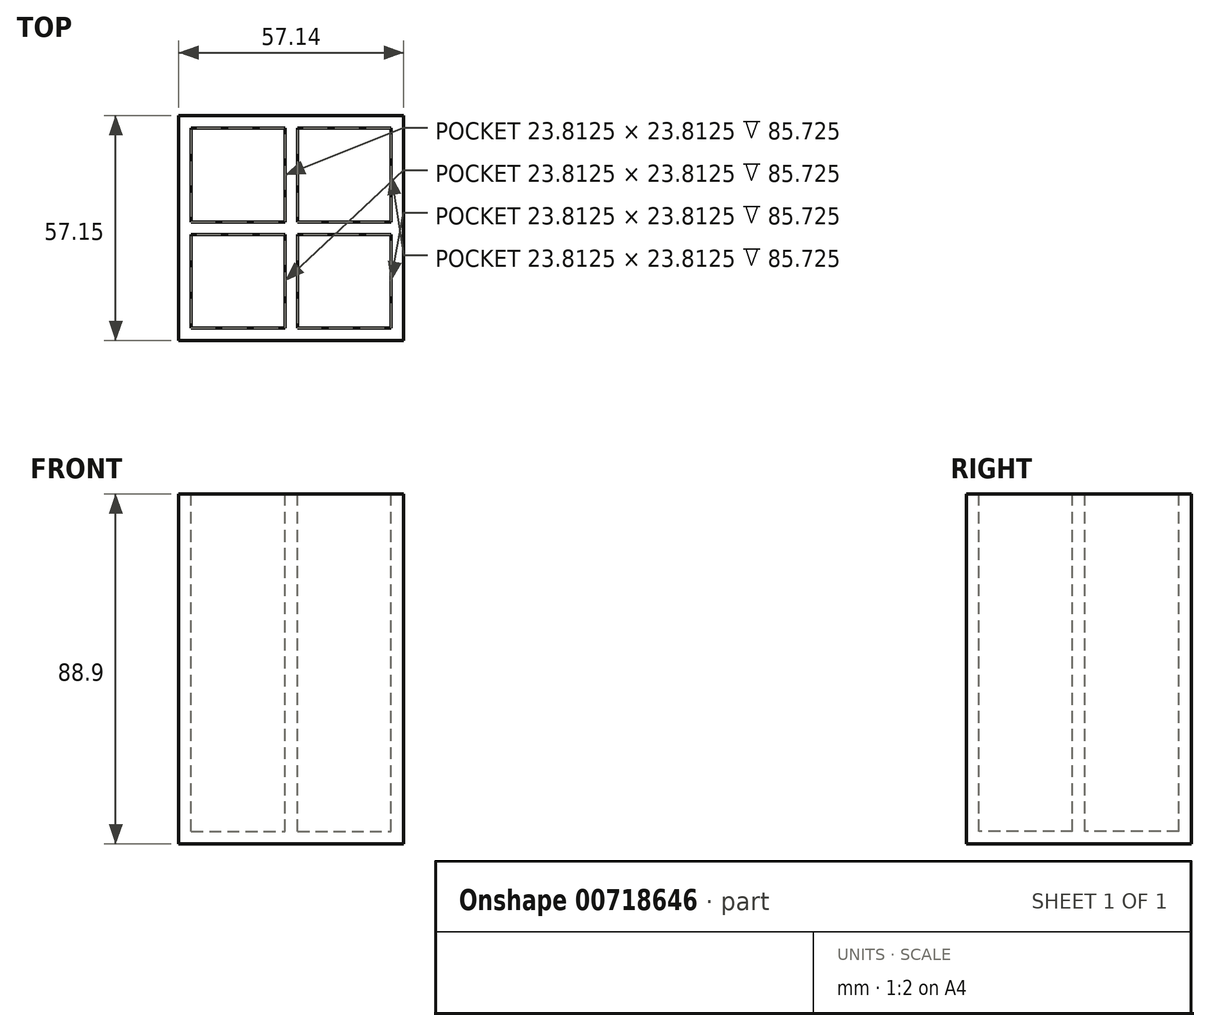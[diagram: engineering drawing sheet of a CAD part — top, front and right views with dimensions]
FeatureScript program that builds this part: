
annotation { "Feature Type Name" : "Feature", "Feature Type Description" : "" }
export const myFeature = defineFeature(function(context is Context, id is Id, definition is map)
    precondition{}
    {
        {
            var Q0;
            Q0=qCreatedBy(makeId("Front.planeOp"),FACE);
            var sketch = newSketch(context, id + "F0", { "sketchPlane" : qUnion([Q0])});
            skLineSegment(sketch, "E0.bottom", {"start": v(28.57, 44.45) * mm, "end": v(-28.58, 44.45) * mm});
            skLineSegment(sketch, "E0.top", {"start": v(28.58, -44.45) * mm, "end": v(-28.57, -44.45) * mm});
            skLineSegment(sketch, "E0.left", {"start": v(28.57, 44.45) * mm, "end": v(28.58, -44.45) * mm});
            skLineSegment(sketch, "E0.right", {"start": v(-28.58, 44.45) * mm, "end": v(-28.57, -44.45) * mm});
            skPoint(sketch, "E0.middle", {"position": v(0, 0) * mm});
            skSolve(sketch);
        }
        {
            var Q0;
            Q0=makeQuery(id+"F0.imprint","IMPRINT",FACE,{"disambiguationData":[TD([[makeQuery(id+"F0.imprint","IMPRINT",EDGE,{"derivedFrom":sQuery(id+"F0.wireOp",EDGE,"E0.bottom")}),1.0]])]});
            extrude(context, id + "F1", {"entities" : qUnion([Q0]), "depth" : 3.17 * mm, "offsetDistance" : 25.4 * mm});
        }
        {
            var Q0;
            Q0=makeQuery(id+"F1.opExtrude","CAP_FACE",FACE,{"disambiguationData":[OSD([sQuery(id+"F0.wireOp",EDGE,"E0.bottom"),sQuery(id+"F0.wireOp",EDGE,"E0.top"),sQuery(id+"F0.wireOp",EDGE,"E0.left"),sQuery(id+"F0.wireOp",EDGE,"E0.right")])],"isStart":true});
            extrude(context, id + "F2", {"entities" : qUnion([Q0]), "operationType" : NewBodyOperationType.ADD, "oppositeDirection" : true, "depth" : 57.15 * mm, "offsetDistance" : 25.4 * mm});
        }
        {
            var Q0;
            {var subQ0=sQuery(id+"F0.wireOp",EDGE,"E0.bottom");Q0=makeQuery(id+"F2.boolean.opBoolean","MERGE",FACE,{"derivedFrom":[makeQuery(id+"F1.opExtrude","SWEPT_FACE",FACE,{"disambiguationData":[OSD([subQ0])]}),makeQuery(id+"F2.opExtrude","SWEPT_FACE",FACE,{"disambiguationData":[OSD([subQ0])]})]});}
            var sketch = newSketch(context, id + "F3", { "sketchPlane" : qUnion([Q0])});
            skLineSegment(sketch, "E1.bottom", {"start": v(-25.4, -3.18) * mm, "end": v(-1.59, -3.18) * mm});
            skLineSegment(sketch, "E1.top", {"start": v(-25.4, -26.99) * mm, "end": v(-1.59, -26.99) * mm});
            skLineSegment(sketch, "E1.left", {"start": v(-25.4, -3.18) * mm, "end": v(-25.4, -26.99) * mm});
            skLineSegment(sketch, "E1.right", {"start": v(-1.59, -3.17) * mm, "end": v(-1.59, -26.99) * mm});
            skSolve(sketch);
        }
        {
            var Q0;
            Q0=makeQuery(id+"F3.imprint","IMPRINT",FACE,{"disambiguationData":[TD([[makeQuery(id+"F3.imprint","IMPRINT",EDGE,{"derivedFrom":sQuery(id+"F3.wireOp",EDGE,"E1.bottom")}),1.0]])]});
            var sketch = newSketch(context, id + "F4", { "sketchPlane" : qUnion([Q0])});
            skLineSegment(sketch, "E2.bottom", {"start": v(1.59, -3.18) * mm, "end": v(25.4, -3.18) * mm});
            skLineSegment(sketch, "E2.top", {"start": v(1.59, -26.99) * mm, "end": v(25.4, -26.99) * mm});
            skLineSegment(sketch, "E2.left", {"start": v(1.59, -3.18) * mm, "end": v(1.59, -26.99) * mm});
            skLineSegment(sketch, "E2.right", {"start": v(25.4, -3.17) * mm, "end": v(25.4, -26.99) * mm});
            skSolve(sketch);
        }
        {
            var Q0;
            Q0=makeQuery(id+"F3.imprint","IMPRINT",FACE,{"disambiguationData":[TD([[makeQuery(id+"F3.imprint","IMPRINT",EDGE,{"derivedFrom":sQuery(id+"F3.wireOp",EDGE,"E1.bottom")}),1.0]])]});
            var sketch = newSketch(context, id + "F5", { "sketchPlane" : qUnion([Q0])});
            skLineSegment(sketch, "E3.bottom", {"start": v(-25.4, -30.16) * mm, "end": v(-1.59, -30.16) * mm});
            skLineSegment(sketch, "E3.top", {"start": v(-25.4, -53.98) * mm, "end": v(-1.59, -53.98) * mm});
            skLineSegment(sketch, "E3.left", {"start": v(-25.4, -30.16) * mm, "end": v(-25.4, -53.98) * mm});
            skLineSegment(sketch, "E3.right", {"start": v(-1.59, -30.16) * mm, "end": v(-1.59, -53.98) * mm});
            skSolve(sketch);
        }
        {
            var Q0;
            Q0=makeQuery(id+"F3.imprint","IMPRINT",FACE,{"disambiguationData":[TD([[makeQuery(id+"F3.imprint","IMPRINT",EDGE,{"derivedFrom":sQuery(id+"F3.wireOp",EDGE,"E1.bottom")}),1.0]])]});
            var sketch = newSketch(context, id + "F6", { "sketchPlane" : qUnion([Q0])});
            skLineSegment(sketch, "E4.bottom", {"start": v(1.59, -30.16) * mm, "end": v(25.4, -30.16) * mm});
            skLineSegment(sketch, "E4.top", {"start": v(1.59, -53.98) * mm, "end": v(25.4, -53.98) * mm});
            skLineSegment(sketch, "E4.left", {"start": v(1.59, -30.16) * mm, "end": v(1.59, -53.98) * mm});
            skLineSegment(sketch, "E4.right", {"start": v(25.4, -30.16) * mm, "end": v(25.4, -53.98) * mm});
            skSolve(sketch);
        }
        {
            var Q0;
            Q0=makeQuery(id+"F4.imprint","IMPRINT",FACE,{"disambiguationData":[TD([[makeQuery(id+"F4.imprint","IMPRINT",EDGE,{"derivedFrom":makeQuery(id+"F3.imprint","IMPRINT",EDGE,{"derivedFrom":sQuery(id+"F3.wireOp",EDGE,"E1.bottom")})}),-1.0]])]});
            var Q1;
            Q1=makeQuery(id+"F5.imprint","IMPRINT",FACE,{"disambiguationData":[TD([[makeQuery(id+"F5.imprint","IMPRINT",EDGE,{"derivedFrom":sQuery(id+"F5.wireOp",EDGE,"E3.bottom")}),-1.0]])]});
            var Q2;
            Q2=makeQuery(id+"F6.imprint","IMPRINT",FACE,{"disambiguationData":[TD([[makeQuery(id+"F6.imprint","IMPRINT",EDGE,{"derivedFrom":sQuery(id+"F6.wireOp",EDGE,"E4.bottom")}),-1.0]])]});
            var Q3;
            Q3=makeQuery(id+"F4.imprint","IMPRINT",FACE,{"disambiguationData":[TD([[makeQuery(id+"F4.imprint","IMPRINT",EDGE,{"derivedFrom":sQuery(id+"F4.wireOp",EDGE,"E2.bottom")}),-1.0]])]});
            extrude(context, id + "F7", {"entities" : qUnion([Q0, Q1, Q2, Q3]), "operationType" : NewBodyOperationType.REMOVE, "oppositeDirection" : true, "depth" : 85.72 * mm, "offsetDistance" : 25.4 * mm});
        }
    });
